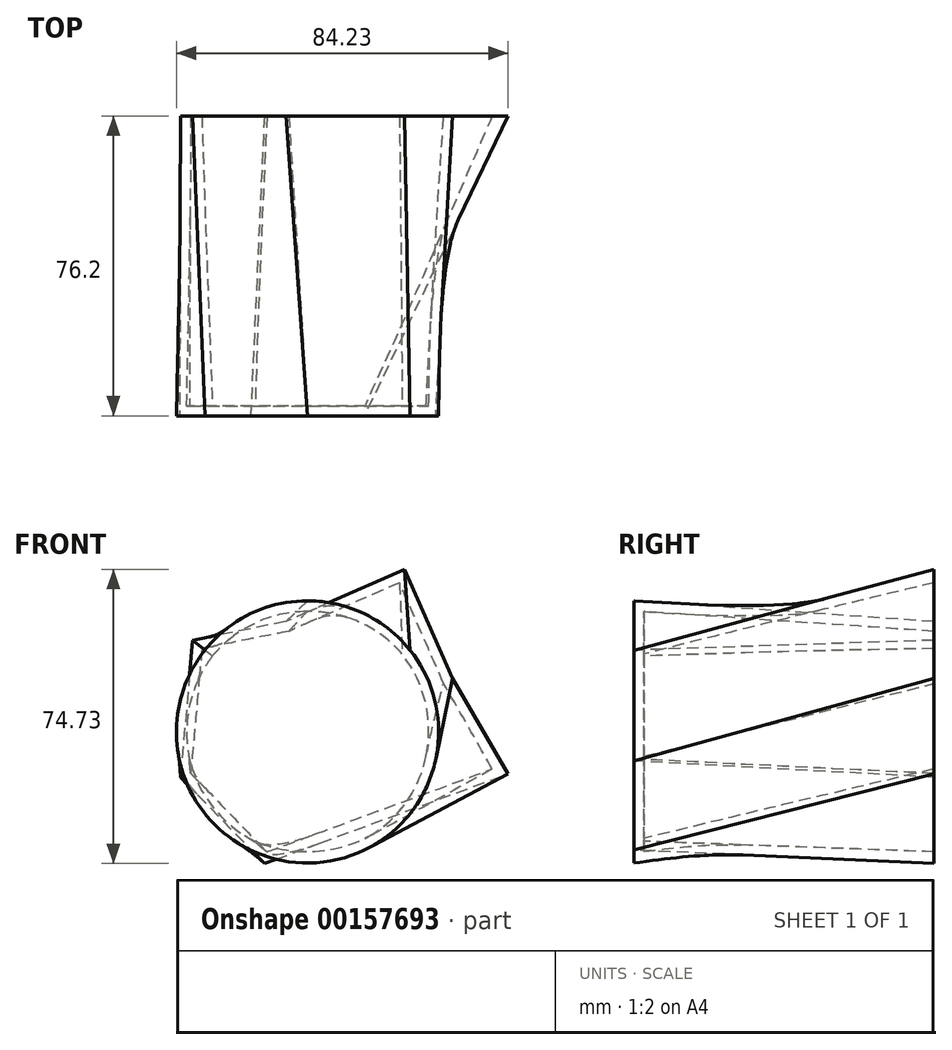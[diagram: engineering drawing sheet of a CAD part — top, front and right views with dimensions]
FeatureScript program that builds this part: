
annotation { "Feature Type Name" : "Feature", "Feature Type Description" : "" }
export const myFeature = defineFeature(function(context is Context, id is Id, definition is map)
    precondition{}
    {
        {
            var Q0;
            Q0=qCreatedBy(makeId("Front.planeOp"),FACE);
            var sketch = newSketch(context, id + "F0", { "sketchPlane" : qUnion([Q0])});
            skLineSegment(sketch, "E0", {"start": v(-29.19, 23.29) * mm, "end": v(-32.3, -11.49) * mm});
            skLineSegment(sketch, "E1", {"start": v(-32.3, -11.49) * mm, "end": v(-10.97, -33.43) * mm});
            skLineSegment(sketch, "E2", {"start": v(-10.97, -33.43) * mm, "end": v(50.92, -10.66) * mm});
            skLineSegment(sketch, "E3", {"start": v(50.92, -10.66) * mm, "end": v(36.85, 13.56) * mm});
            skLineSegment(sketch, "E4", {"start": v(36.85, 13.56) * mm, "end": v(24.63, 41.3) * mm});
            skLineSegment(sketch, "E5", {"start": v(24.63, 41.3) * mm, "end": v(-5.5, 28.03) * mm});
            skLineSegment(sketch, "E6", {"start": v(-5.5, 28.03) * mm, "end": v(-29.19, 23.29) * mm});
            skSolve(sketch);
        }
        {
            var Q0;
            Q0=qCreatedBy(makeId("Front.planeOp"),FACE);
            cPlane(context, id + "F1", {"entities" : qUnion([Q0]), "cplaneType" : CPlaneType.OFFSET, "offset" : 76.2 * mm, "width" : 152.4 * mm, "height" : 152.4 * mm});
        }
        {
            var Q0;
            Q0=qCreatedBy(id+"F1.planeOp",FACE);
            var sketch = newSketch(context, id + "F2", { "sketchPlane" : qUnion([Q0])});
            skCircle(sketch, "E7", {"center": v(0, 0) * mm, "radius": 33.31 * mm});
            skSolve(sketch);
        }
        {
            var Q0;
            Q0=makeQuery(id+"F0.imprint","IMPRINT",FACE,{"disambiguationData":[TD([[makeQuery(id+"F0.imprint","IMPRINT",EDGE,{"derivedFrom":sQuery(id+"F0.wireOp",EDGE,"E0")}),1.0]])]});
            var Q1;
            Q1=makeQuery(id+"F2.imprint","IMPRINT",FACE,{"disambiguationData":[TD([[makeQuery(id+"F2.imprint","IMPRINT",EDGE,{"derivedFrom":sQuery(id+"F2.wireOp",EDGE,"E7")}),1.0]])]});
            loft(context, id + "F3", {"sheetProfilesArray" : [{ "sheetProfileEntities" : qUnion([Q0]) }, { "sheetProfileEntities" : qUnion([Q1]) }]});
        }
        {
            var Q0;
            Q0=makeQuery(id+"F3.opLoft","CAP_FACE",FACE,{"disambiguationData":[OSD([makeQuery(id+"F0.imprint","IMPRINT",FACE,{"disambiguationData":[TD([[makeQuery(id+"F0.imprint","IMPRINT",EDGE,{"derivedFrom":sQuery(id+"F0.wireOp",EDGE,"E0")}),1.0]])]})])],"isStart":true});
            shell(context, id + "F4", {"entities" : qUnion([Q0]), "thickness" : 2.54 * mm});
        }
    });
